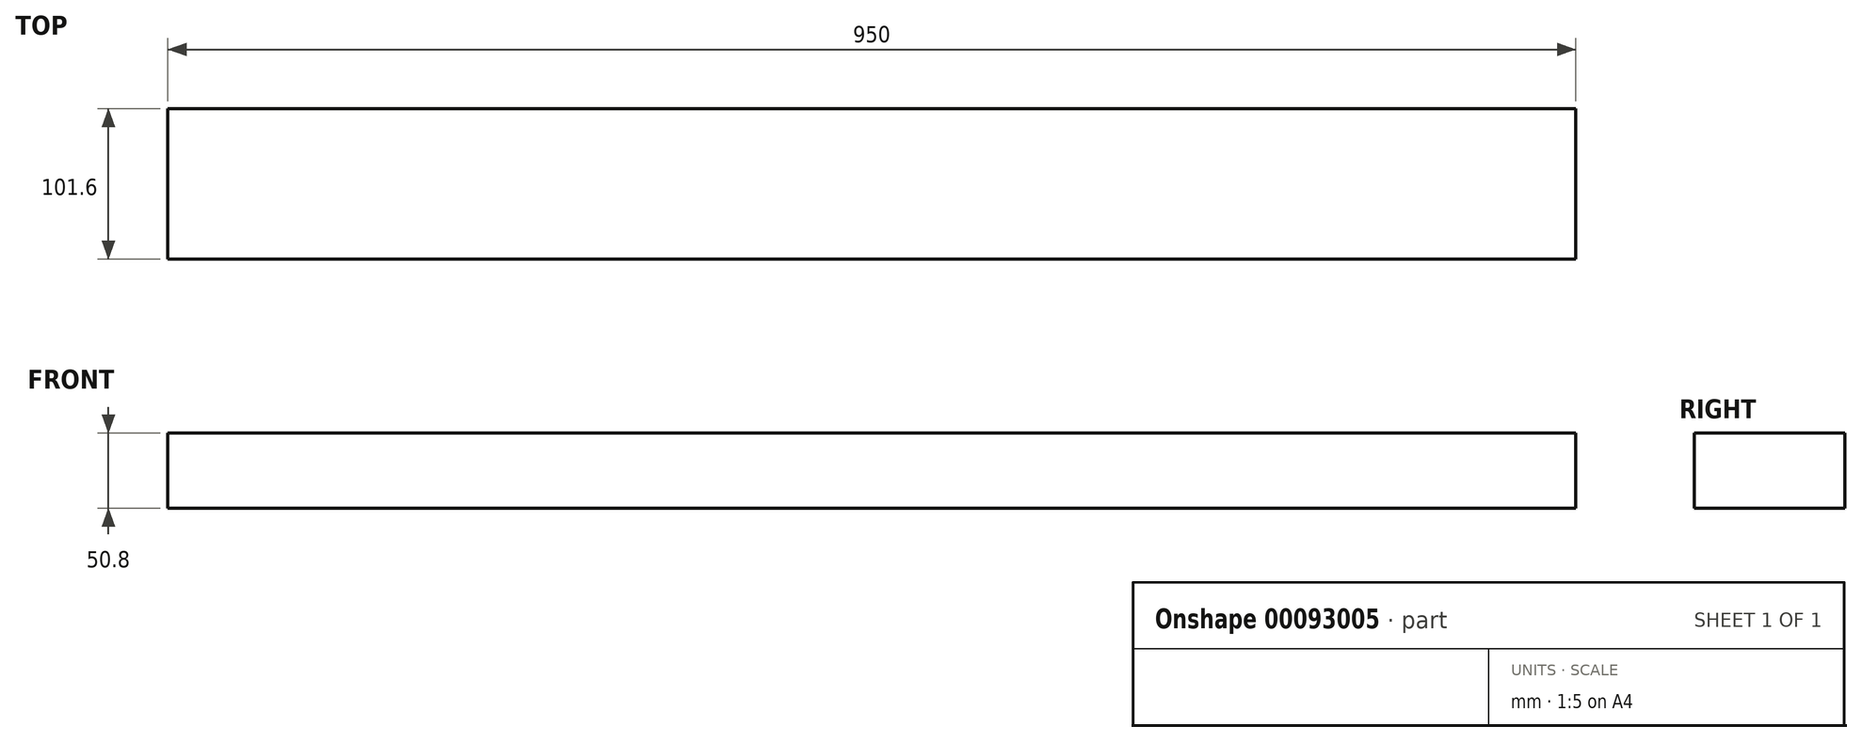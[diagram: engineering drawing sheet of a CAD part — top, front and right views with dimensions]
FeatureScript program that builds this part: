
annotation { "Feature Type Name" : "Feature", "Feature Type Description" : "" }
export const myFeature = defineFeature(function(context is Context, id is Id, definition is map)
    precondition{}
    {
        {
            var Q0;
            Q0=qCreatedBy(makeId("Right.planeOp"),FACE);
            var sketch = newSketch(context, id + "F0", { "sketchPlane" : qUnion([Q0])});
            skLineSegment(sketch, "E0.bottom", {"start": v(-50.8, 50.8) * mm, "end": v(50.8, 50.8) * mm});
            skLineSegment(sketch, "E0.top", {"start": v(-50.8, 0) * mm, "end": v(50.8, 0) * mm});
            skLineSegment(sketch, "E0.left", {"start": v(-50.8, 50.8) * mm, "end": v(-50.8, 0) * mm});
            skLineSegment(sketch, "E0.right", {"start": v(50.8, 50.8) * mm, "end": v(50.8, 0) * mm});
            skSolve(sketch);
        }
        {
            var Q0;
            Q0=makeQuery(id+"F0.imprint","IMPRINT",FACE,{"disambiguationData":[TD([[makeQuery(id+"F0.imprint","IMPRINT",EDGE,{"derivedFrom":sQuery(id+"F0.wireOp",EDGE,"E0.bottom")}),-1.0]])]});
            extrude(context, id + "F1", {"entities" : qUnion([Q0]), "endBound" : BoundingType.SYMMETRIC, "depth" : 1000 * mm});
        }
        {
            var Q0;
            Q0=makeQuery(id+"F1.opExtrude","SWEPT_FACE",FACE,{"disambiguationData":[OSD([sQuery(id+"F0.wireOp",EDGE,"E0.bottom")])]});
            var sketch = newSketch(context, id + "F2", { "sketchPlane" : qUnion([Q0])});
            skLineSegment(sketch, "E1.bottom", {"start": v(-500, -50.8) * mm, "end": v(-475, -50.8) * mm});
            skLineSegment(sketch, "E1.top", {"start": v(-500, 50.8) * mm, "end": v(-475, 50.8) * mm});
            skLineSegment(sketch, "E1.left", {"start": v(-500, -50.8) * mm, "end": v(-500, 50.8) * mm});
            skLineSegment(sketch, "E1.right", {"start": v(-475, -50.8) * mm, "end": v(-475, 50.8) * mm});
            skLineSegment(sketch, "E2.bottom", {"start": v(500, -50.8) * mm, "end": v(475, -50.8) * mm});
            skLineSegment(sketch, "E2.top", {"start": v(500, 50.8) * mm, "end": v(475, 50.8) * mm});
            skLineSegment(sketch, "E2.left", {"start": v(500, -50.8) * mm, "end": v(500, 50.8) * mm});
            skLineSegment(sketch, "E2.right", {"start": v(475, -50.8) * mm, "end": v(475, 50.8) * mm});
            skSolve(sketch);
        }
        {
            var Q0;
            Q0 = qSketchRegion(id + "F2", true);
            extrude(context, id + "F3", {"entities" : qUnion([Q0]), "operationType" : NewBodyOperationType.REMOVE, "oppositeDirection" : true, "depth" : 66.05 * mm});
        }
    });
